# Revit family: glorious_slim_410-9652
name_source: partatom
category: Leuchten
revit_build: Autodesk Revit 2016 (Build: 20190508_0715(x64)
units: mm (PartAtom-declared; Revit-internal decimal feet)

## family parameters
Basisbauteil = Fläche
Beim Laden mit Abzugskörper schneiden = Nein
Bemaßung runder Anschluss = Durchmesser verwenden
Gemeinsam genutzt = Nein
Lichtquelle = Nein
Raumberechnungspunkt = Nein
Teiletyp = Normal

## types (1)
- 410-9652-D01-H27 (4 x LED, 405.68 lm, 3.1 W, 2700K)
    Beschreibung = GLORIOUS SLIM
    CIE Flux Codes = 48 79 96 100 78
    Color Rendering = 1A/90…99
    Color Temperature = 2700K
    Height = 90 mm
    Hersteller = Prolicht
    Lamp Light Flux = 405.68 lm
    Lamp Power = 3.1 W
    Lamp count = 4
    Lampe = 4 x LED
    Length = 576 mm
    Luminous efficacy = 103 lm/W
    ModVariant = Nein
    Modell = 410-9652
    Mounting Place = Ceiling
    Mounting Type = Pendant
    Number of Poles = 1
    OnlyDefault = Ja
    Power Factor = 1
    Product Name = GLORIOUS SLIM
    Product group = Suspended lights
    ProductGroupID = 941
    Protection Class = Protection class
    Protection Degree = Degree of protection
    RLX_Detail_Level = 1
    RlxData = <blob elided: 55921 chars, md5=f838d544>
    Scheinlast = 198 VA
    Socket = socket
    Standby Power = 0 W
    System Light Flux = 20355 lm
    System Power = 198 W
    Typenbild = 410-9652.jpg
    Typenkommentare = DIFFUSER Opal (01),LED COLOUR DIR 2700 K (27)
    URL = http://relux.com
    VarID = 410-9652-d01-h27
    Voltage = 0 V
    Vorgabe-Ansicht = 1800 mm
    Weight = 0.00 kg
    Width = 65 mm

## geometry (parser evidence)
native form markers: Blend x4, Sweep x46
no freeform markers — native parametric forms only
